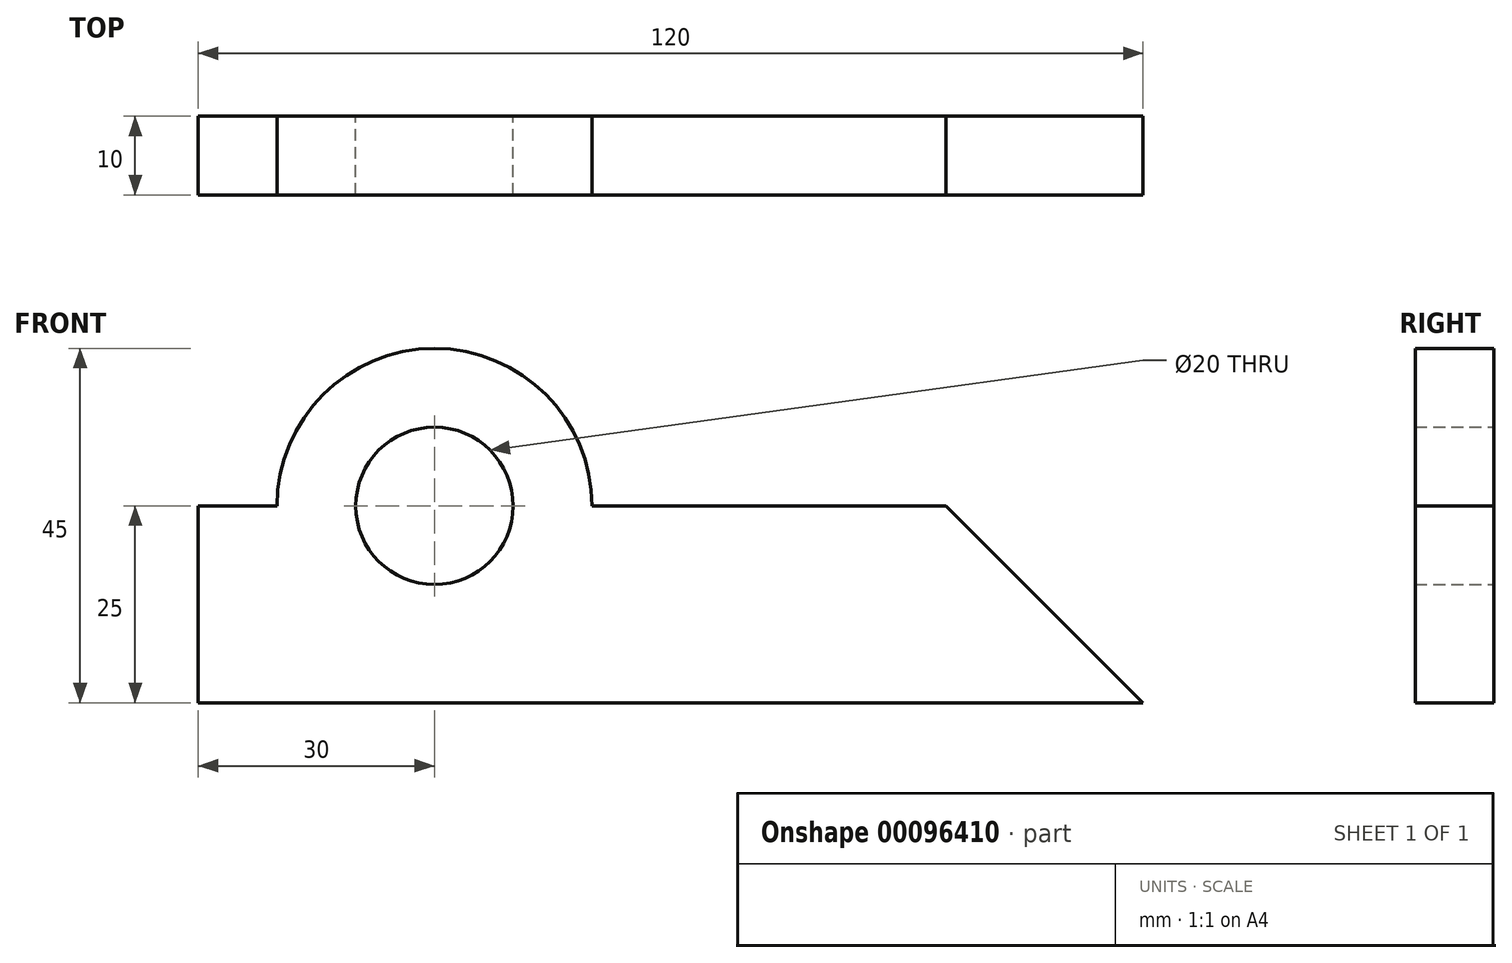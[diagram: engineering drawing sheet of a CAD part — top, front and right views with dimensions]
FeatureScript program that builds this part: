
annotation { "Feature Type Name" : "Feature", "Feature Type Description" : "" }
export const myFeature = defineFeature(function(context is Context, id is Id, definition is map)
    precondition{}
    {
        {
            var Q0;
            Q0=qCreatedBy(makeId("Front.planeOp"),FACE);
            var sketch = newSketch(context, id + "F0", { "sketchPlane" : qUnion([Q0])});
            skLineSegment(sketch, "E0", {"start": v(0, 0) * mm, "end": v(0, 25) * mm});
            skLineSegment(sketch, "E1", {"start": v(0, 25) * mm, "end": v(10, 25) * mm});
            skLineSegment(sketch, "E2", {"start": v(50, 25) * mm, "end": v(95, 25) * mm});
            skLineSegment(sketch, "E3", {"start": v(95, 25) * mm, "end": v(120, 0) * mm});
            skLineSegment(sketch, "E4", {"start": v(120, 0) * mm, "end": v(0, 0) * mm});
            skArc(sketch, "E5", {"start": v(50, 25) * mm, "mid": v(30, 45) * mm, "end": v(10, 25) * mm});
            skCircle(sketch, "E6", {"center": v(30, 25) * mm, "radius": 10 * mm});
            skSolve(sketch);
        }
        {
            var Q0;
            Q0=makeQuery(id+"F0.imprint","IMPRINT",FACE,{"disambiguationData":[TD([[makeQuery(id+"F0.imprint","IMPRINT",EDGE,{"derivedFrom":sQuery(id+"F0.wireOp",EDGE,"E0")}),-1.0]])]});
            extrude(context, id + "F1", {"entities" : qUnion([Q0]), "depth" : 10 * mm});
        }
    });
